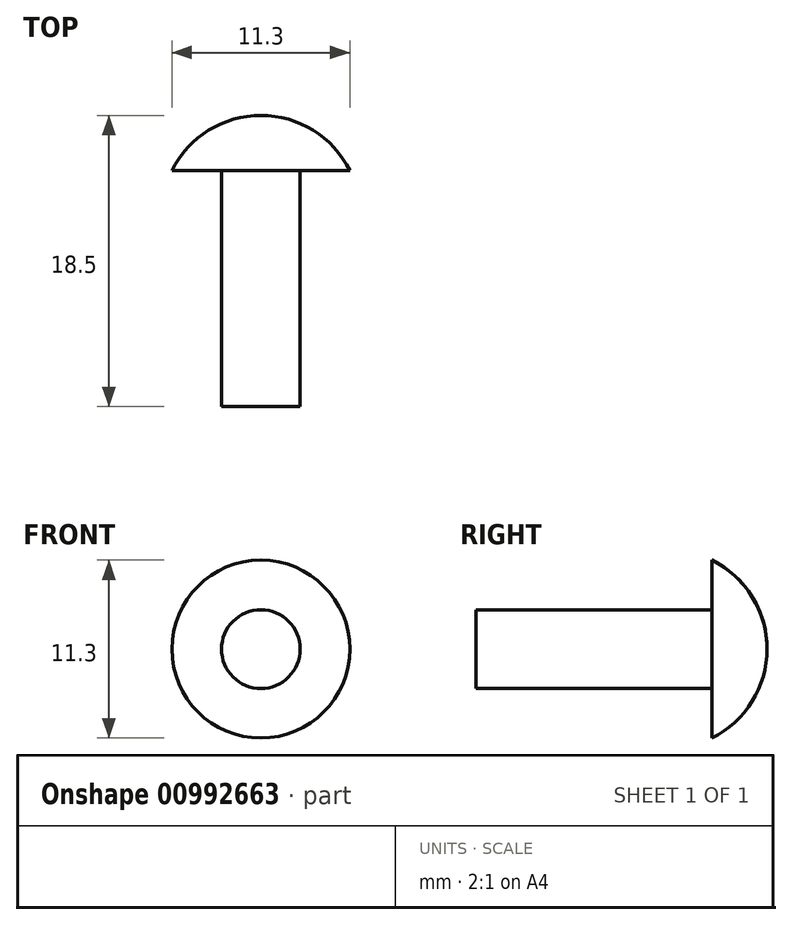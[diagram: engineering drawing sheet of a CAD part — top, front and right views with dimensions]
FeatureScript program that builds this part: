
annotation { "Feature Type Name" : "Feature", "Feature Type Description" : "" }
export const myFeature = defineFeature(function(context is Context, id is Id, definition is map)
    precondition{}
    {
        {
            var Q0;
            Q0=qCreatedBy(makeId("Right.planeOp"),FACE);
            var sketch = newSketch(context, id + "F0", { "sketchPlane" : qUnion([Q0])});
            skLineSegment(sketch, "E0", {"start": v(0, 0) * mm, "end": v(18.5, 0) * mm});
            skLineSegment(sketch, "E1", {"start": v(0, 0) * mm, "end": v(0, 2.5) * mm});
            skLineSegment(sketch, "E2", {"start": v(0, 2.5) * mm, "end": v(15, 2.5) * mm});
            skLineSegment(sketch, "E3", {"start": v(15, 2.5) * mm, "end": v(15, 5.65) * mm});
            skArc(sketch, "E4", {"start": v(18.5, 0) * mm, "mid": v(17.55, 3.32) * mm, "end": v(15, 5.65) * mm});
            skLineSegment(sketch, "E5", {"start": v(18.5, 0) * mm, "end": v(18.5, 5.65) * mm, "construction": true});
            skLineSegment(sketch, "E6", {"start": v(15, 5.65) * mm, "end": v(18.5, 5.65) * mm});
            skSolve(sketch);
        }
        {
            var Q0;
            Q0=makeQuery(id+"F0.imprint","IMPRINT",FACE,{"disambiguationData":[TD([[makeQuery(id+"F0.imprint","IMPRINT",EDGE,{"derivedFrom":sQuery(id+"F0.wireOp",EDGE,"E0")}),1.0]])]});
            var Q1;
            Q1=sQuery(id+"F0.wireOp",EDGE,"E0");
            revolve(context, id + "F1", {"surfaceOperationType" : NewSurfaceOperationType.NEW, "entities" : qUnion([Q0]), "axis" : qUnion([Q1]), "revolveType" : RevolveType.FULL});
        }
    });
